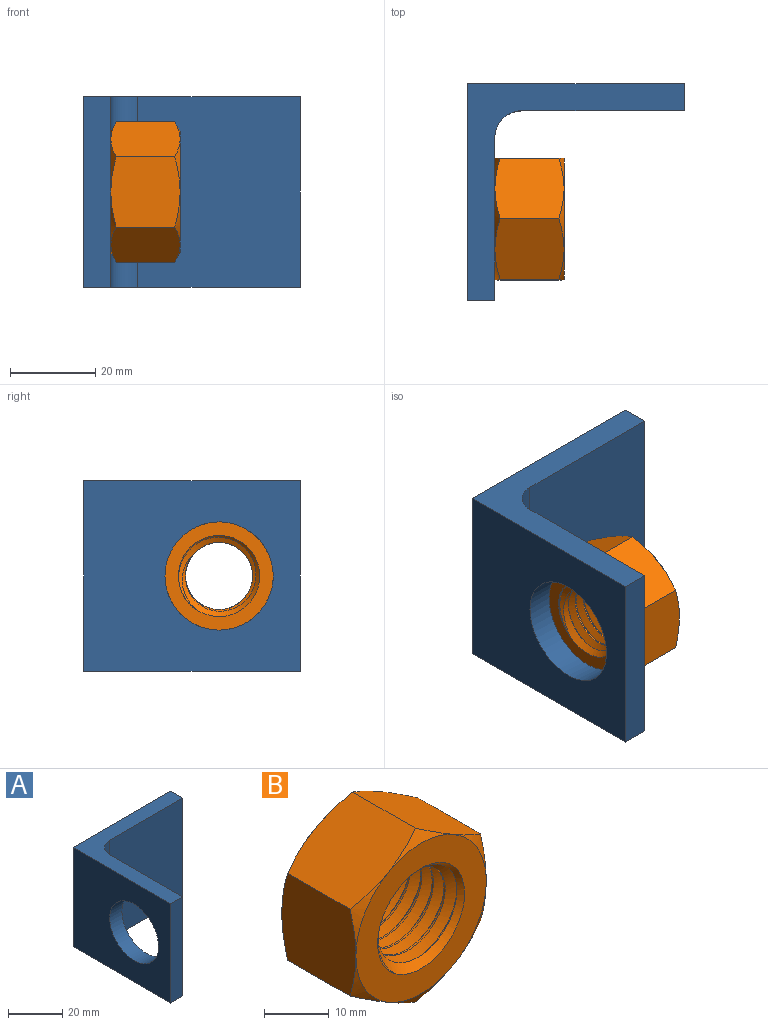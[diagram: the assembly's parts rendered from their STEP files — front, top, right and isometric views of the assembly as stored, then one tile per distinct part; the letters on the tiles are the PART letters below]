
ASSEMBLY  parts=2 mates=1
PART A: 10 faces, bbox 50.8x50.8x44.6 mm
  f0: plane 50.8x44.6mm, normal (0,1,0), area 2265.8mm2, adj f1,f6,f7,f8
  f1: plane 50.8x44.6mm, normal (-1,0,0), area 1759.1mm2, adj f0,f2,f7,f8,f9
  f2: plane 44.6x6.35mm, normal (0,-1,0), area 283.2mm2, adj f1,f3,f7,f8
  f3: plane 44.6x38.1mm, normal (1,0,0), area 1192.6mm2, adj f2,f4,f7,f8,f9
  f4: cylinder r=6.35mm len=44.6mm, axis (0,0,-1), area 444.9mm2, adj f3,f5,f7,f8
  f5: plane 44.6x38.1mm, normal (0,-1,0), area 1699.4mm2, adj f4,f6,f7,f8
  f6: plane 44.6x6.35mm, normal (1,0,0), area 283.2mm2, adj f0,f5,f7,f8
  f7: plane 50.8x50.8mm, normal (0,0,1), area 613.5mm2, adj f0,f1,f2,f3,f4,f5,f6
  f8: plane 50.8x50.8mm, normal (0,0,-1), area 613.5mm2, adj f0,f1,f2,f3,f4,f5,f6
  f9: cylinder r=12.7mm len=25.4mm, axis (1,0,0), area 506.7mm2, adj f1,f3
PART B: 26 faces, bbox 34.4x19.5x34.4 mm
  f0: plane 28.58x28.58mm, normal (0,-1,0), area 356.3mm2, adj f7,f12,f13,f14,f15,f16,f17,f18
  f1: plane 17.63x15.64mm, normal (-0.5,0,0.87), area 254mm2, adj f2,f6,f13,f18,f21,f22
  f2: plane 17.87x17.64mm, normal (-1,0,0), area 254mm2, adj f1,f3,f17,f18,f22,f23
  f3: plane 17.63x15.64mm, normal (-0.5,0,-0.87), area 254mm2, adj f2,f4,f16,f17,f23,f24
  f4: plane 17.63x15.64mm, normal (0.5,0,-0.87), area 254mm2, adj f3,f5,f15,f16,f24,f25
  f5: plane 17.87x17.64mm, normal (1,0,0), area 254mm2, adj f4,f6,f14,f15,f20,f25
  f6: plane 17.63x15.64mm, normal (0.5,0,0.87), area 254mm2, adj f1,f5,f13,f14,f20,f21
  f7: cylinder r=9.53mm len=19.05mm, axis (0,1,0), area 117.5mm2, adj f0,f8,f9,f11
  f8: plane 28.58x28.58mm, normal (0,1,0), area 356.3mm2, adj f7,f19,f20,f21,f22,f23,f24,f25
  f9: bspline ~19.04x19.01mm, area 601.9mm2, adj f7,f10,f12,f19
  f10: cylinder r=7.88mm len=15.75mm, axis (0,-1,0), area 134.1mm2, adj f9,f11,f12,f19
  f11: bspline ~20.03x19.05mm, area 602.3mm2, adj f7,f10,f12,f19
  f12: cone r=8.89mm half-angle=45deg, axis (0,-1,0), area 65.2mm2, adj f0,f9,f10,f11
  f13: cone r=14.29mm half-angle=60deg, axis (0,1,0), area 20.1mm2, adj f0,f1,f6
  f14: cone r=14.29mm half-angle=60deg, axis (0,1,0), area 20.1mm2, adj f0,f5,f6
  f15: cone r=14.29mm half-angle=60deg, axis (0,1,0), area 20.1mm2, adj f0,f4,f5
  f16: cone r=14.29mm half-angle=60deg, axis (0,1,0), area 20.1mm2, adj f0,f3,f4
  f17: cone r=14.29mm half-angle=60deg, axis (0,1,0), area 20.1mm2, adj f0,f2,f3
  f18: cone r=14.29mm half-angle=60deg, axis (0,1,0), area 20.1mm2, adj f0,f1,f2
  f19: cone r=8.89mm half-angle=45deg, axis (0,1,0), area 65.3mm2, adj f8,f9,f10,f11
  f20: cone r=14.29mm half-angle=60deg, axis (0,-1,0), area 20.1mm2, adj f5,f6,f8
  f21: cone r=14.29mm half-angle=60deg, axis (0,-1,0), area 20.1mm2, adj f1,f6,f8
  f22: cone r=14.29mm half-angle=60deg, axis (0,-1,0), area 20.1mm2, adj f1,f2,f8
  f23: cone r=14.29mm half-angle=60deg, axis (0,-1,0), area 20.1mm2, adj f2,f3,f8
  f24: cone r=14.29mm half-angle=60deg, axis (0,-1,0), area 20.1mm2, adj f3,f4,f8
  f25: cone r=14.29mm half-angle=60deg, axis (0,-1,0), area 20.1mm2, adj f4,f5,f8
PLACE A t=(-17.57,32.57,-18.33)mm
PLACE B rot(axis=(0,0,-1),90deg) t=(-3.08,0.82,3.97)mm
MATE fastened B.f7 <-> A.f9  axis (-1,0,0) through (-11.22,0.82,3.97)mm
